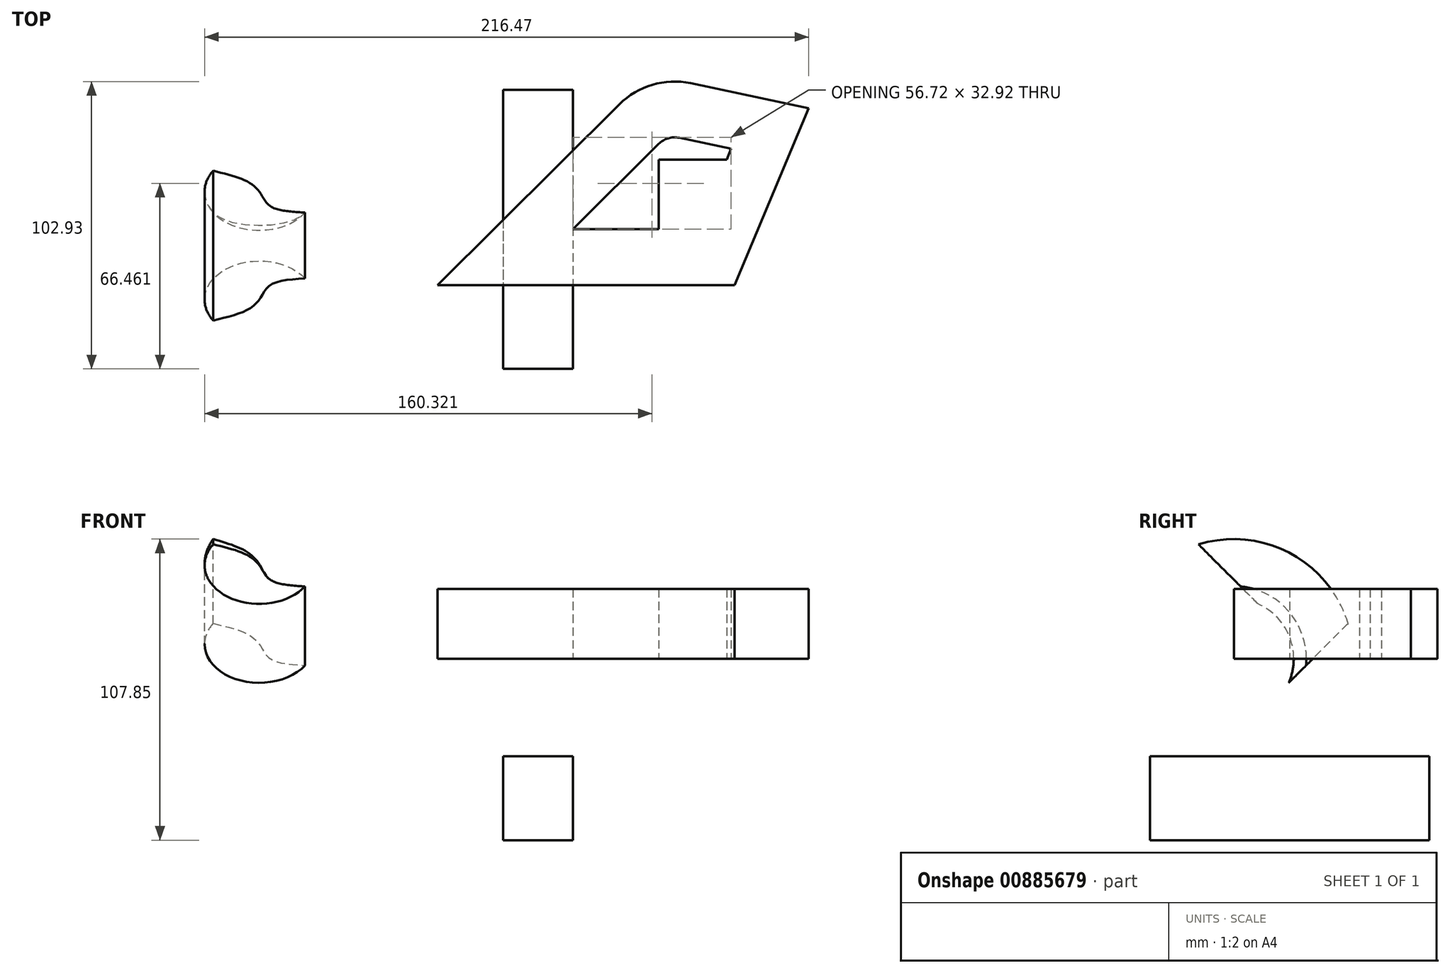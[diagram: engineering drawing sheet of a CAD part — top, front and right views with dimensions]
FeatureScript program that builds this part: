
annotation { "Feature Type Name" : "Feature", "Feature Type Description" : "" }
export const myFeature = defineFeature(function(context is Context, id is Id, definition is map)
    precondition{}
    {
        {
            var Q0;
            Q0=qCreatedBy(makeId("Top.planeOp"),FACE);
            var sketch = newSketch(context, id + "F0", { "sketchPlane" : qUnion([Q0])});
            skLineSegment(sketch, "E0", {"start": v(0, 0) * mm, "end": v(30.78, 30.6) * mm});
            skLineSegment(sketch, "E1", {"start": v(38.07, 32.76) * mm, "end": v(56.72, 28.83) * mm});
            skLineSegment(sketch, "E2", {"start": v(56.72, 28.83) * mm, "end": v(44.65, 0) * mm});
            skLineSegment(sketch, "E3", {"start": v(44.65, 0) * mm, "end": v(0, 0) * mm});
            skLineSegment(sketch, "E4", {"start": v(-57.94, -37.2) * mm, "end": v(-23.83, -37.2) * mm});
            skLineSegment(sketch, "E5", {"start": v(-18.83, -42.2) * mm, "end": v(-18.83, -68.39) * mm});
            skPoint(sketch, "E6.visualSharp", {"position": v(-18.83, -37.2) * mm});
            skArc(sketch, "E6.filletArc", {"start": v(-18.83, -42.2) * mm, "mid": v(-20.3, -38.67) * mm, "end": v(-23.83, -37.2) * mm});
            skPoint(sketch, "E7.visualSharp", {"position": v(33.84, 33.65) * mm});
            skArc(sketch, "E7.filletArc", {"start": v(38.07, 32.76) * mm, "mid": v(34.15, 32.6) * mm, "end": v(30.78, 30.6) * mm});
            skArc(sketch, "E8.0", {"start": v(42.19, 52.33) * mm, "mid": v(28.48, 51.78) * mm, "end": v(16.68, 44.78) * mm});
            skLineSegment(sketch, "E8.1", {"start": v(-48.48, -20) * mm, "end": v(16.68, 44.78) * mm});
            skLineSegment(sketch, "E8.2", {"start": v(42.19, 52.33) * mm, "end": v(84.51, 43.42) * mm});
            skLineSegment(sketch, "E8.3", {"start": v(84.51, 43.42) * mm, "end": v(57.95, -20) * mm});
            skLineSegment(sketch, "E8.4", {"start": v(57.95, -20) * mm, "end": v(-48.48, -20) * mm});
            skSolve(sketch);
        }
        {
            var Q0;
            Q0 = qSketchRegion(id + "F0", true);
            extrude(context, id + "F1", {"entities" : qUnion([Q0]), "depth" : 25 * mm, "offsetDistance" : 25 * mm});
        }
        {
            var Q0;
            Q0=qCreatedBy(makeId("Front.planeOp"),FACE);
            var sketch = newSketch(context, id + "F2", { "sketchPlane" : qUnion([Q0])});
            skLineSegment(sketch, "E9.0.0", {"start": v(38.07, 0) * mm, "end": v(56.72, 0) * mm});
            skLineSegment(sketch, "E9.0.1", {"start": v(56.72, 0) * mm, "end": v(56.72, 25) * mm});
            skLineSegment(sketch, "E9.0.2", {"start": v(56.72, 25) * mm, "end": v(38.07, 25) * mm});
            skLineSegment(sketch, "E9.0.3", {"start": v(38.07, 25) * mm, "end": v(38.07, 0) * mm});
            skLineSegment(sketch, "E10.0.0", {"start": v(30.78, 0) * mm, "end": v(38.07, 0) * mm});
            skLineSegment(sketch, "E10.0.1", {"start": v(38.07, 0) * mm, "end": v(38.07, 25) * mm});
            skLineSegment(sketch, "E10.0.2", {"start": v(38.07, 25) * mm, "end": v(30.78, 25) * mm});
            skLineSegment(sketch, "E10.0.3", {"start": v(30.78, 25) * mm, "end": v(30.78, 0) * mm});
            skSolve(sketch);
        }
        {
            var Q0;
            Q0 = qSketchRegion(id + "F2", true);
            extrude(context, id + "F3", {"entities" : qUnion([Q0]), "operationType" : NewBodyOperationType.ADD, "oppositeDirection" : true, "depth" : 25 * mm, "offsetDistance" : 25 * mm});
        }
        {
            var Q0;
            Q0=qCreatedBy(makeId("Front.planeOp"),FACE);
            var sketch = newSketch(context, id + "F4", { "sketchPlane" : qUnion([Q0])});
            skArc(sketch, "E11", {"start": v(-128.9, 37.9) * mm, "mid": v(-123.02, 10.93) * mm, "end": v(-96, 16.59) * mm});
            skFitSpline(sketch, "E12", {"points": [v(-128.9, 37.9) * mm, v(-118.07, 33.46) * mm, v(-112.36, 27.38) * mm, v(-108.18, 19.77) * mm, v(-96, 16.59) * mm], "startDerivative": vector(43.9, -14.42) * mm, "endDerivative": vector(51.67, -4.91) * mm});
            skSolve(sketch);
        }
        {
            var Q0;
            Q0=makeQuery(id+"F4.imprint","IMPRINT",FACE,{"disambiguationData":[TD([[makeQuery(id+"F4.imprint","IMPRINT",EDGE,{"derivedFrom":sQuery(id+"F4.wireOp",EDGE,"E11")}),1.0]])]});
            var Q1;
            Q1=makeQuery(id+"F1.opExtrude","CAP_EDGE",EDGE,{"disambiguationData":[OSD([sQuery(id+"F0.wireOp",EDGE,"E8.4")])],"isStart":true});
            revolve(context, id + "F5", {"surfaceOperationType" : NewSurfaceOperationType.NEW, "entities" : qUnion([Q0]), "axis" : qUnion([Q1]), "revolveType" : RevolveType.SYMMETRIC, "angle" : 90 * degree});
        }
        {
            var Q0;
            Q0=qCreatedBy(makeId("Right.planeOp"),FACE);
            var sketch = newSketch(context, id + "F6", { "sketchPlane" : qUnion([Q0])});
            skLineSegment(sketch, "E13.bottom", {"start": v(50, -65) * mm, "end": v(-50, -65) * mm});
            skLineSegment(sketch, "E13.top", {"start": v(50, -35) * mm, "end": v(-50, -35) * mm});
            skLineSegment(sketch, "E13.left", {"start": v(50, -65) * mm, "end": v(50, -35) * mm});
            skLineSegment(sketch, "E13.right", {"start": v(-50, -65) * mm, "end": v(-50, -35) * mm});
            skSolve(sketch);
        }
        {
            var Q0;
            Q0=makeQuery(id+"F6.imprint","IMPRINT",FACE,{"disambiguationData":[TD([[makeQuery(id+"F6.imprint","IMPRINT",EDGE,{"derivedFrom":sQuery(id+"F6.wireOp",EDGE,"E13.bottom")}),-1.0]])]});
            var Q1;
            Q1=sQuery(id+"F6.wireOp",EDGE,"E13.left");
            extrude(context, id + "F7", {"entities" : qUnion([Q0]), "surfaceEntities" : qUnion([Q1]), "oppositeDirection" : true, "depth" : 25 * mm, "offsetDistance" : 25 * mm});
        }
    });
